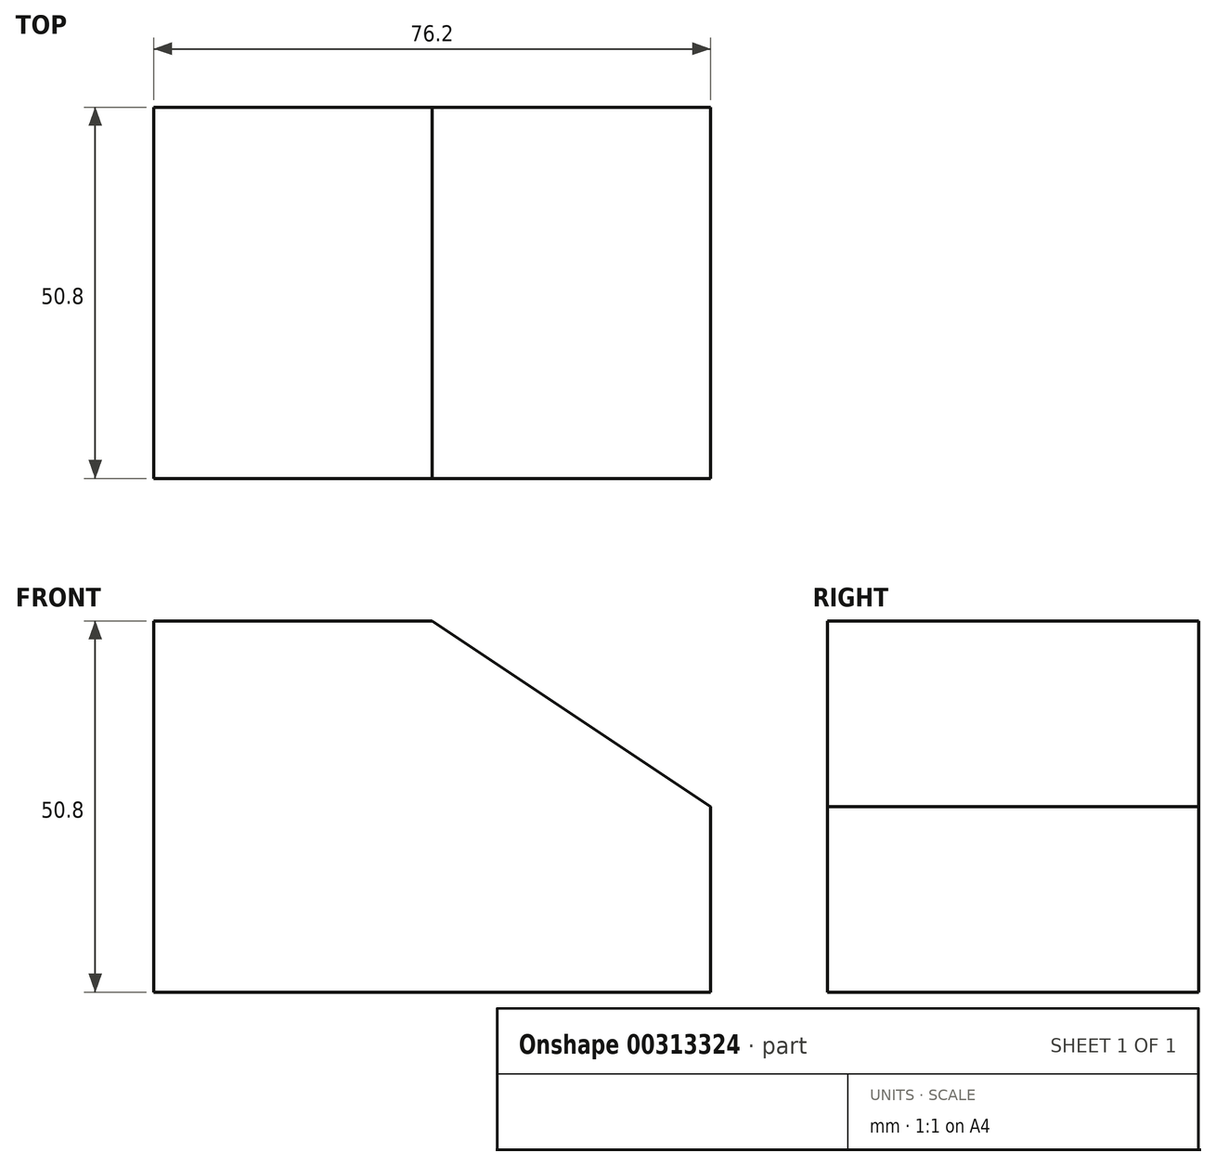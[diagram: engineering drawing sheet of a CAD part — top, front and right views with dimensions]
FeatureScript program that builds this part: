
annotation { "Feature Type Name" : "Feature", "Feature Type Description" : "" }
export const myFeature = defineFeature(function(context is Context, id is Id, definition is map)
    precondition{}
    {
        {
            var Q0;
            Q0=qCreatedBy(makeId("Front.planeOp"),FACE);
            var sketch = newSketch(context, id + "F0", { "sketchPlane" : qUnion([Q0])});
            skLineSegment(sketch, "E0", {"start": v(-72.74, 25.24) * mm, "end": v(-72.74, -25.56) * mm});
            skLineSegment(sketch, "E1", {"start": v(-72.74, 25.24) * mm, "end": v(-34.64, 25.24) * mm});
            skLineSegment(sketch, "E2", {"start": v(-72.74, -25.56) * mm, "end": v(3.46, -25.56) * mm});
            skLineSegment(sketch, "E3", {"start": v(3.46, -25.56) * mm, "end": v(3.46, -0.16) * mm});
            skLineSegment(sketch, "E4", {"start": v(-34.64, 25.24) * mm, "end": v(3.46, -0.16) * mm});
            skSolve(sketch);
        }
        {
            var Q0;
            Q0=makeQuery(id+"F0.imprint","IMPRINT",FACE,{"disambiguationData":[TD([[makeQuery(id+"F0.imprint","IMPRINT",EDGE,{"derivedFrom":sQuery(id+"F0.wireOp",EDGE,"E0")}),1.0]])]});
            extrude(context, id + "F1", {"entities" : qUnion([Q0]), "depth" : 50.8 * mm});
        }
    });
